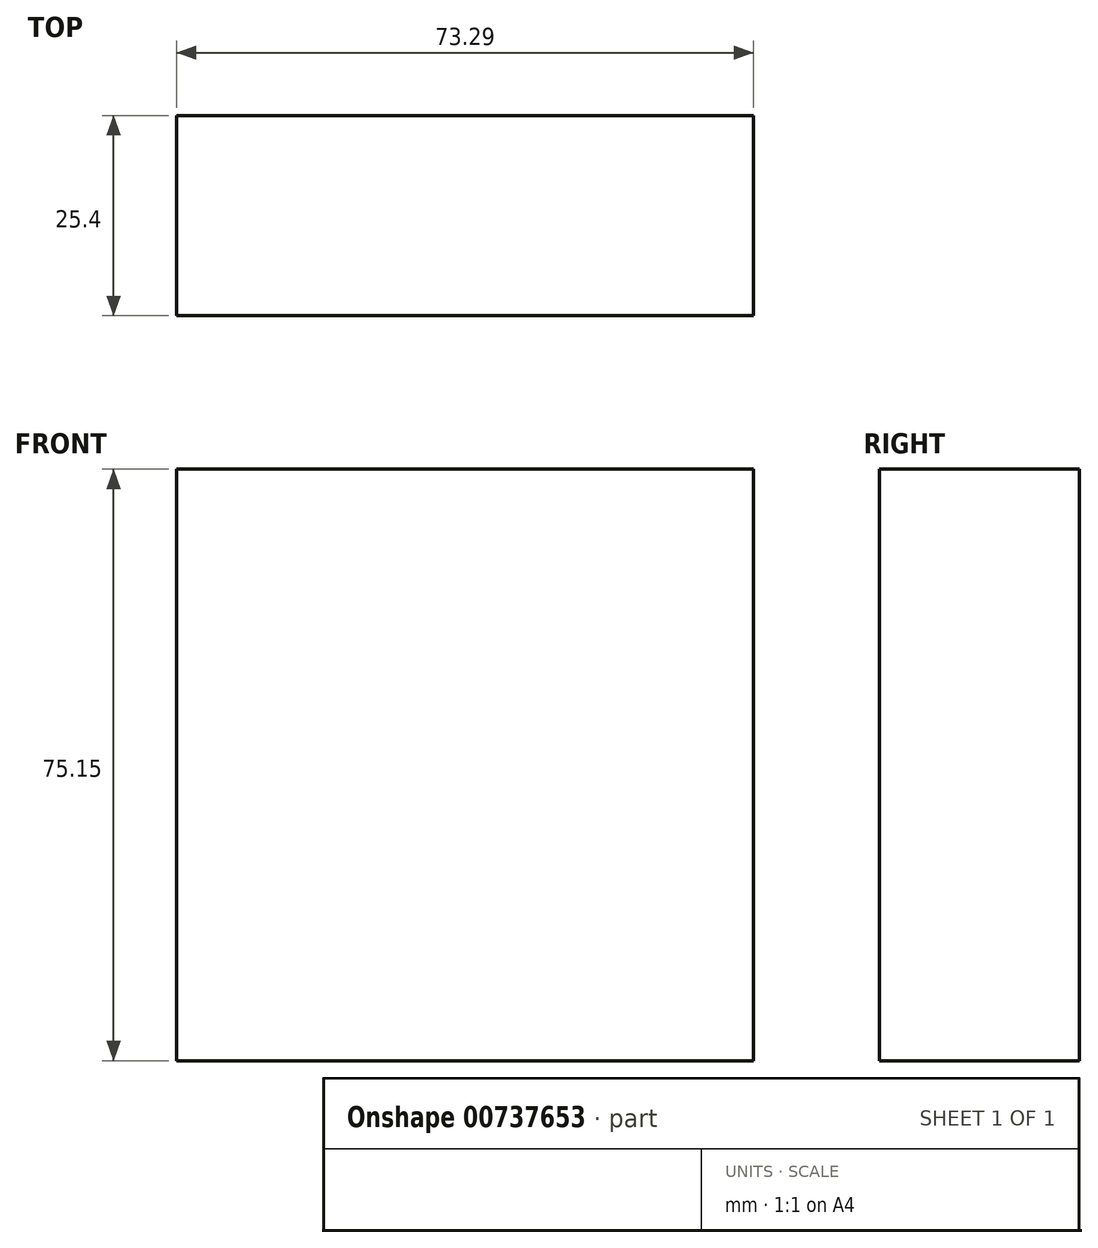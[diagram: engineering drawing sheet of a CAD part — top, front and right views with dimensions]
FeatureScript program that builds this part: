
annotation { "Feature Type Name" : "Feature", "Feature Type Description" : "" }
export const myFeature = defineFeature(function(context is Context, id is Id, definition is map)
    precondition{}
    {
        {
            var Q0;
            Q0=qCreatedBy(makeId("Front.planeOp"),FACE);
            var sketch = newSketch(context, id + "F0", { "sketchPlane" : qUnion([Q0])});
            skLineSegment(sketch, "E0.bottom", {"start": v(0, -75.15) * mm, "end": v(-73.3, -75.15) * mm});
            skLineSegment(sketch, "E0.top", {"start": v(0, 0) * mm, "end": v(-73.3, 0) * mm});
            skLineSegment(sketch, "E0.left", {"start": v(0, -75.15) * mm, "end": v(0, 0) * mm});
            skLineSegment(sketch, "E0.right", {"start": v(-73.3, -75.15) * mm, "end": v(-73.3, 0) * mm});
            skSolve(sketch);
        }
        {
            var Q0;
            Q0 = qSketchRegion(id + "F0", true);
            extrude(context, id + "F1", {"entities" : qUnion([Q0]), "depth" : 25.4 * mm, "offsetDistance" : 25.4 * mm});
        }
    });
